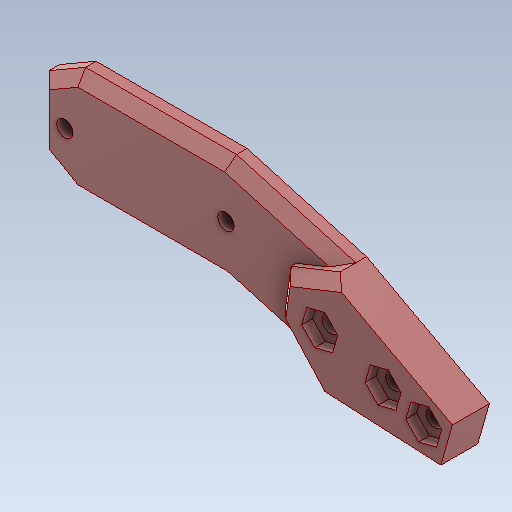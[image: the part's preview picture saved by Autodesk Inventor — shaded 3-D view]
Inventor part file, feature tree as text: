
AUTODESK INVENTOR PART (.ipt)
format: ipt  version: 2020 (Build 240168000, 168)  size: 197,120 bytes
history: native  units: in
note: dims shown in document units (in); Inventor stores cm internally (conversion verified against a paired STEP export)
features: sketch x4, other x3, extrude x1
ambient origin geometry x8: Origin, YZ Plane, XZ Plane, XY Plane, X Axis, Y Axis, Z Axis, Center Point
bodies: Solid1 (feature_tree)
feature tree (8):
  other  "Fibula.ipt"
  extrude  "Extrusion1"  Depth=0.2756in
  other  "Solid1::Fibula.ipt"
  other  "TaggingFeature1"
  sketch  "Sketch1"  dims[d0=0.3937in d1=0.2756in]
  sketch  "Sketch3"  dims[d2=0.2756in]
  sketch  "Sketch4"  dims[d4=0.3937in d5=0.0in]
  sketch  "Sketch5"  dims[d6=0.2756in]
